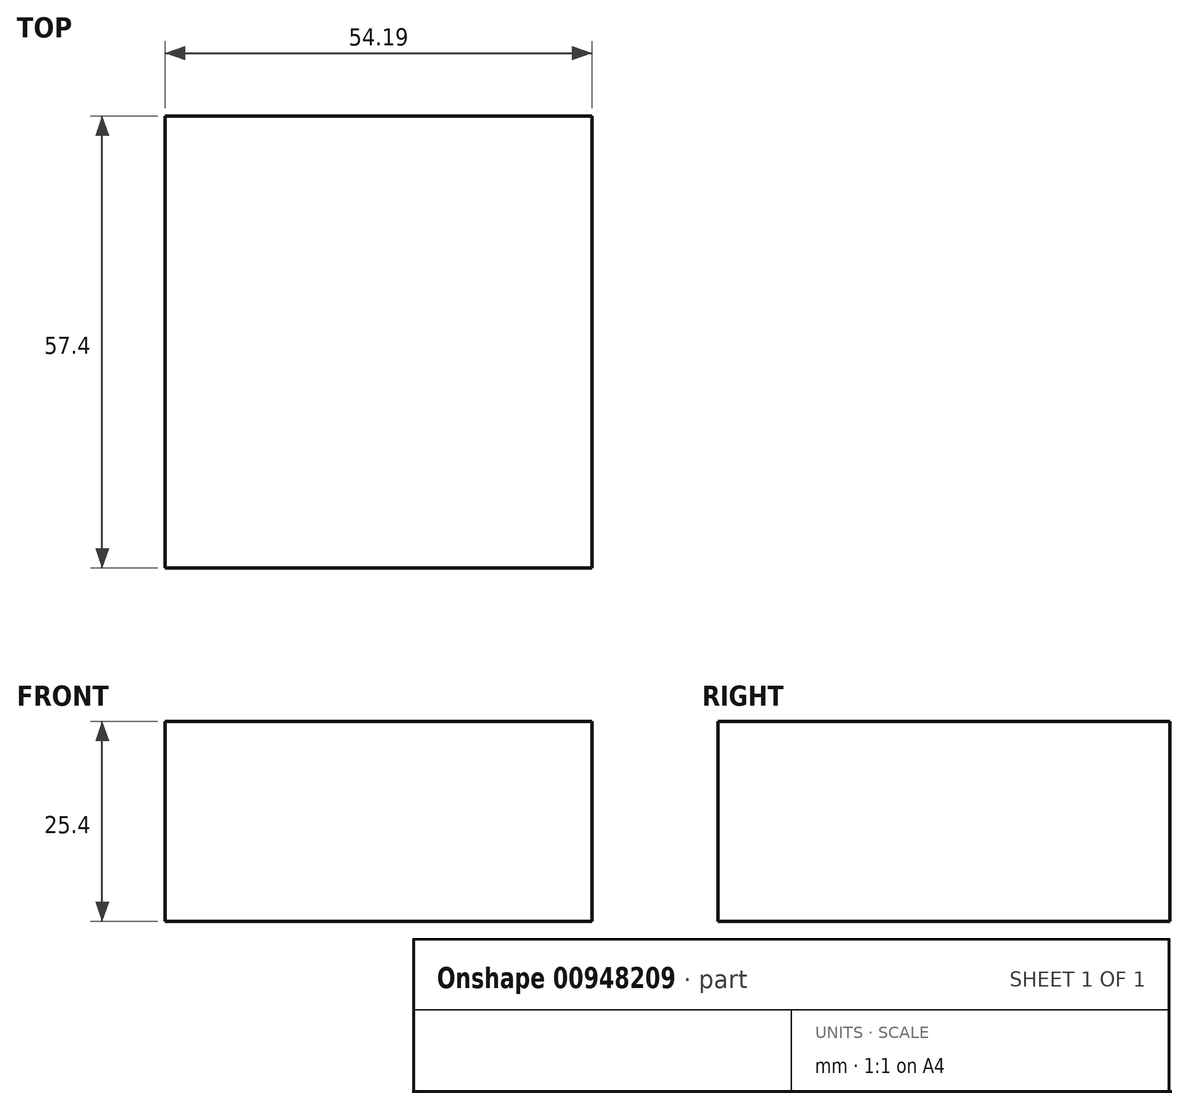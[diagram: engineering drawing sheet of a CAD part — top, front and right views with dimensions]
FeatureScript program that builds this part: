
annotation { "Feature Type Name" : "Feature", "Feature Type Description" : "" }
export const myFeature = defineFeature(function(context is Context, id is Id, definition is map)
    precondition{}
    {
        {
            var Q0;
            Q0=qCreatedBy(makeId("Top.planeOp"),FACE);
            var sketch = newSketch(context, id + "F0", { "sketchPlane" : qUnion([Q0])});
            skLineSegment(sketch, "E0.bottom", {"start": v(-26.75, 18.83) * mm, "end": v(27.44, 18.83) * mm});
            skLineSegment(sketch, "E0.top", {"start": v(-26.75, -38.57) * mm, "end": v(27.44, -38.57) * mm});
            skLineSegment(sketch, "E0.left", {"start": v(-26.75, 18.83) * mm, "end": v(-26.75, -38.57) * mm});
            skLineSegment(sketch, "E0.right", {"start": v(27.44, 18.83) * mm, "end": v(27.44, -38.57) * mm});
            skSolve(sketch);
        }
        {
            var Q0;
            Q0 = qSketchRegion(id + "F0", true);
            extrude(context, id + "F1", {"entities" : qUnion([Q0]), "depth" : 25.4 * mm, "offsetDistance" : 25.4 * mm});
        }
    });
